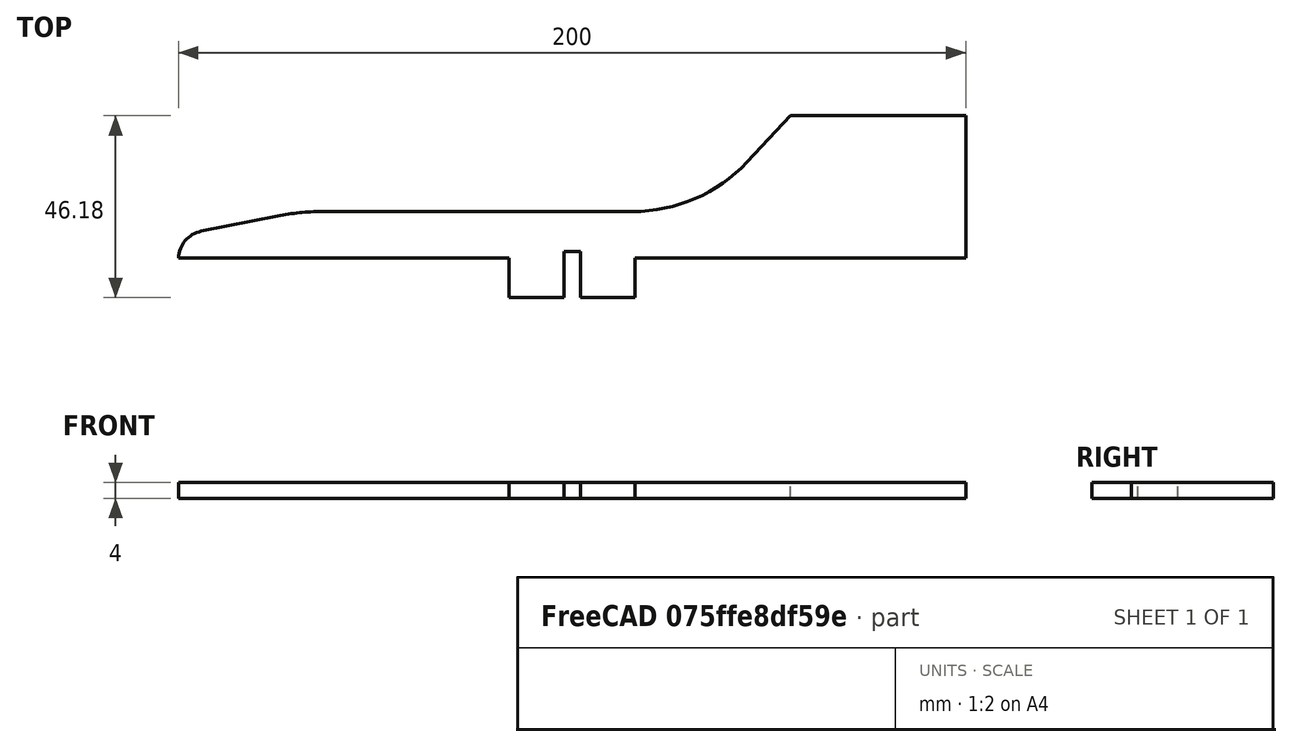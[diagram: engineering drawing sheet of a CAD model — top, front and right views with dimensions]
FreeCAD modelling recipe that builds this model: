
FCSTD DOCUMENT  (FreeCAD 0.18R16131 (Git))
Label: solo_banderuola4mm
License: All rights reserved
LicenseURL: http://en.wikipedia.org/wiki/All_rights_reserved
objects: Sketcher::SketchObject×1, PartDesign::Pad×1, PartDesign::Body×1
note: 4 computed .brp shape members not serialized (recipe doc carries the construction recipe); baked Part::Feature solids carry a one-line shape summary decoded from their .brp

FEATURE [Sketcher::SketchObject] CopySketch004
  sketch-geometry (22):
    g0: LineSegment StartX=-94.2446 StartY=6.83669 StartZ=0 EndX=-74.9207 EndY=10.7048 EndZ=0
    g1: LineSegment StartX=-63.6033 StartY=11.8264 StartZ=0 EndX=-42.5521 EndY=11.8264 EndZ=0
    g2: LineSegment StartX=-42.5521 StartY=11.8264 StartZ=0 EndX=15.3719 EndY=11.8264 EndZ=0
    g3: LineSegment StartX=44.4109 StartY=24.4067 StartZ=0 EndX=55.4445 EndY=36.1754 EndZ=0
    g4: LineSegment StartX=55.4445 StartY=36.1754 StartZ=0 EndX=100 EndY=36.1754 EndZ=0
    g5: LineSegment StartX=100 StartY=36.1754 StartZ=0 EndX=100 EndY=0 EndZ=0
    g6: LineSegment StartX=100 StartY=0 StartZ=0 EndX=16 EndY=0 EndZ=0
    g7: ArcOfCircle CenterX=-63.6033 CenterY=-45.8333 CenterZ=0 NormalX=0 NormalY=0 NormalZ=1 AngleXU=0 Radius=57.6597 StartAngle=1.5708 EndAngle=1.76836
    g8: ArcOfCircle CenterX=15.3719 CenterY=51.6318 CenterZ=0 NormalX=0 NormalY=0 NormalZ=1 AngleXU=0 Radius=39.8055 StartAngle=4.71239 EndAngle=5.53002
    g9: ArcOfCircle CenterX=-92.8385 CenterY=-0.187922 CenterZ=0 NormalX=0 NormalY=0 NormalZ=1 AngleXU=0 Radius=7.16397 StartAngle=1.76836 EndAngle=3.11536
    g10: GeomPoint X=16 Y=0 Z=0
    g11: GeomPoint X=-16 Y=0 Z=0
    g12: LineSegment StartX=-16 StartY=0 StartZ=0 EndX=-16 EndY=-10 EndZ=0
    g13: LineSegment StartX=-16 StartY=-10 StartZ=0 EndX=-2.15 EndY=-10 EndZ=0
    g14: LineSegment StartX=16 StartY=-10 StartZ=0 EndX=16 EndY=0 EndZ=0
    g15: LineSegment StartX=-16 StartY=0 StartZ=0 EndX=-100 EndY=1e-16 EndZ=0
    g16: GeomPoint X=-2.15 Y=-10 Z=0
    g17: GeomPoint X=2.15 Y=-10 Z=0
    g18: LineSegment StartX=-2.15 StartY=-10 StartZ=0 EndX=-2.15 EndY=1.64739 EndZ=0
    g19: LineSegment StartX=-2.15 StartY=1.64739 StartZ=0 EndX=2.15 EndY=1.64739 EndZ=0
    g20: LineSegment StartX=2.15 StartY=1.64739 StartZ=0 EndX=2.15 EndY=-10 EndZ=0
    g21: LineSegment StartX=2.15 StartY=-10 StartZ=0 EndX=16 EndY=-10 EndZ=0
  constraints (45):
    c: Horizontal(g1)
    c: Coincident(g1,g2)
    c: Horizontal(g2)
    c: Coincident(g3,g4)
    c: Horizontal(g4)
    c: Coincident(g4,g5)
    c: PointOnObject(g5,g-1)
    c: Vertical(g5)
    c: Coincident(g5,g6)
    c: Horizontal(g6)
    c: Tangent(g0,g7) = 1.5708
    c: Tangent(g1,g7) = 1.5708
    c: Tangent(g2,g8) = -1.5708
    c: Tangent(g3,g8) = -1.5708
    c: Tangent(g0,g9) = 1.5708
    c: Coincident(g15,g9) = 1.5708
    c: DistanceX(g15,g6) = 200
    c: DistanceX(g-1,g5) = 100
    c: PointOnObject(g10,g6)
    c: DistanceX(g11,g10) = 32
    c: Symmetric(g10,g11,g-2)
    c: Coincident(g12,g11)
    c: Vertical(g12)
    c: Coincident(g12,g13)
    c: Horizontal(g13)
    c: Coincident(g21,g14)
    c: Vertical(g14)
    c: Coincident(g14,g10)
    c: PointOnObject(g6,g14)
    c: PointOnObject(g15,g12)
    c: Tangent(g6,g15)
    c: PointOnObject(g16,g13)
    c: DistanceY(g14,g14) = 10
    c: Symmetric(g16,g17,g-2)
    c: Coincident(g18,g16)
    c: Vertical(g18)
    c: Coincident(g18,g19)
    c: Horizontal(g19)
    c: Coincident(g19,g20)
    c: Coincident(g20,g17)
    c: Vertical(g20)
    c: PointOnObject(g13,g18)
    c: PointOnObject(g21,g20)
    c: Tangent(g13,g21)
    c: DistanceX(g13,g17) = 4.3
FEATURE [PartDesign::Pad] Pad
  Length = 4
  Length2 = 100
  Midplane = true
  Profile = -> CopySketch004
  Type = 0
FEATURE [PartDesign::Body] Body001
  Group = -> [Pad]
  Origin = -> Origin001
  Tip = -> Pad
